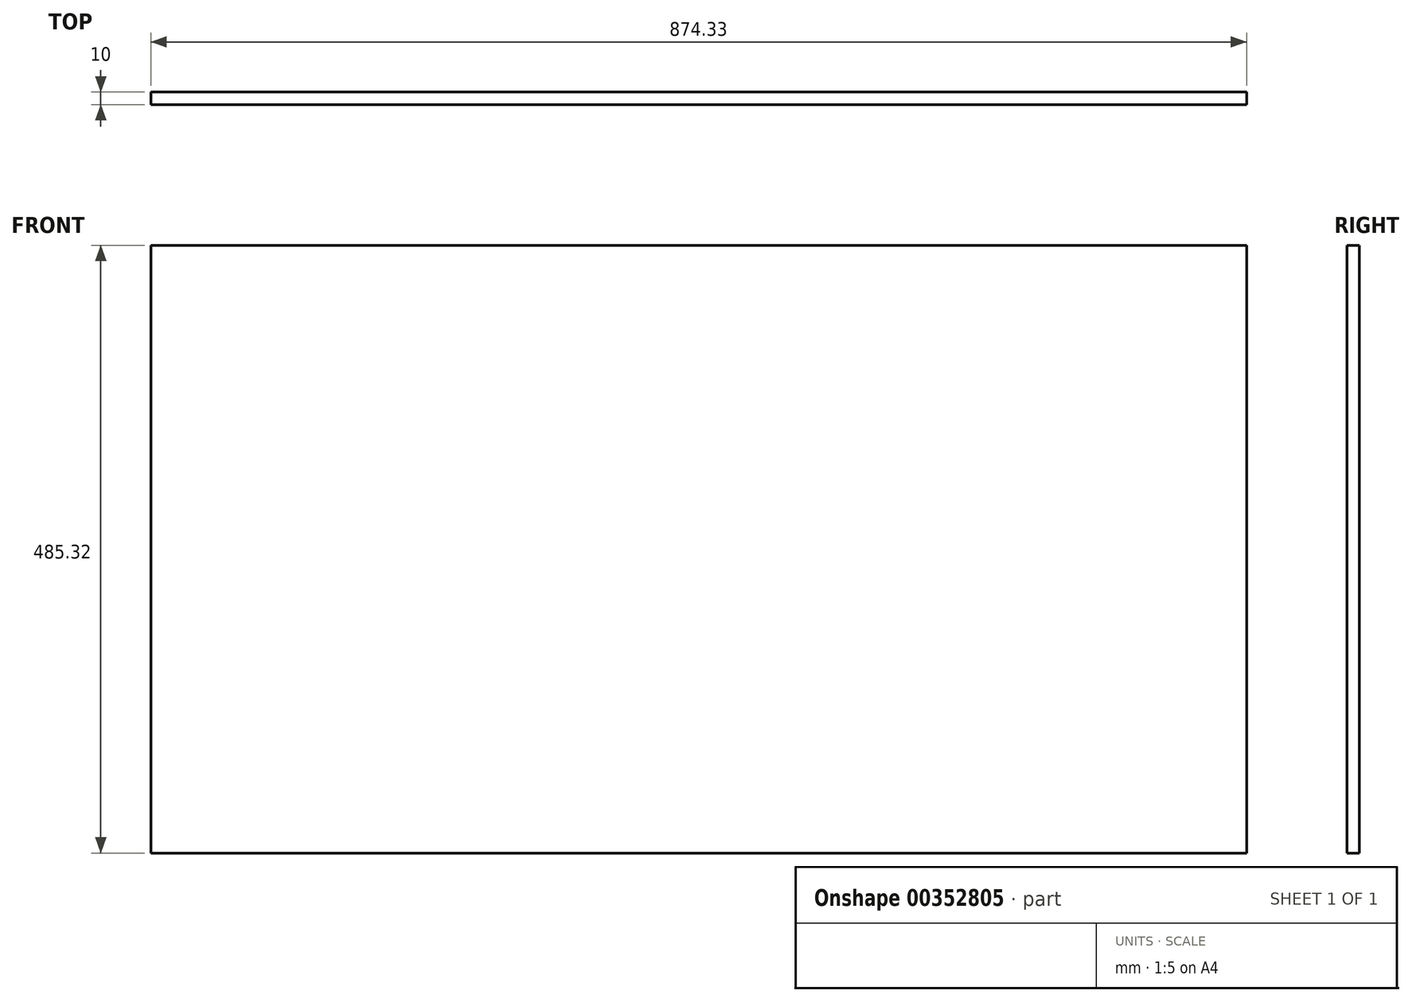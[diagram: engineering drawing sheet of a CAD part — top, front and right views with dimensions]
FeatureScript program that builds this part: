
annotation { "Feature Type Name" : "Feature", "Feature Type Description" : "" }
export const myFeature = defineFeature(function(context is Context, id is Id, definition is map)
    precondition{}
    {
        {
            var Q0;
            Q0=qCreatedBy(makeId("Front.planeOp"),FACE);
            var sketch = newSketch(context, id + "F0", { "sketchPlane" : qUnion([Q0])});
            skLineSegment(sketch, "E0.bottom", {"start": v(-389.41, 197.16) * mm, "end": v(484.92, 197.16) * mm});
            skLineSegment(sketch, "E0.top", {"start": v(-389.41, -288.16) * mm, "end": v(484.92, -288.16) * mm});
            skLineSegment(sketch, "E0.left", {"start": v(-389.41, 197.16) * mm, "end": v(-389.41, -288.16) * mm});
            skLineSegment(sketch, "E0.right", {"start": v(484.92, 197.16) * mm, "end": v(484.92, -288.16) * mm});
            skLineSegment(sketch, "E1", {"start": v(-389.41, 197.16) * mm, "end": v(484.92, -288.16) * mm});
            skSolve(sketch);
        }
        {
            var Q0;
            Q0 = qSketchRegion(id + "F0", true);
            extrude(context, id + "F1", {"entities" : qUnion([Q0]), "depth" : 10 * mm});
        }
    });
